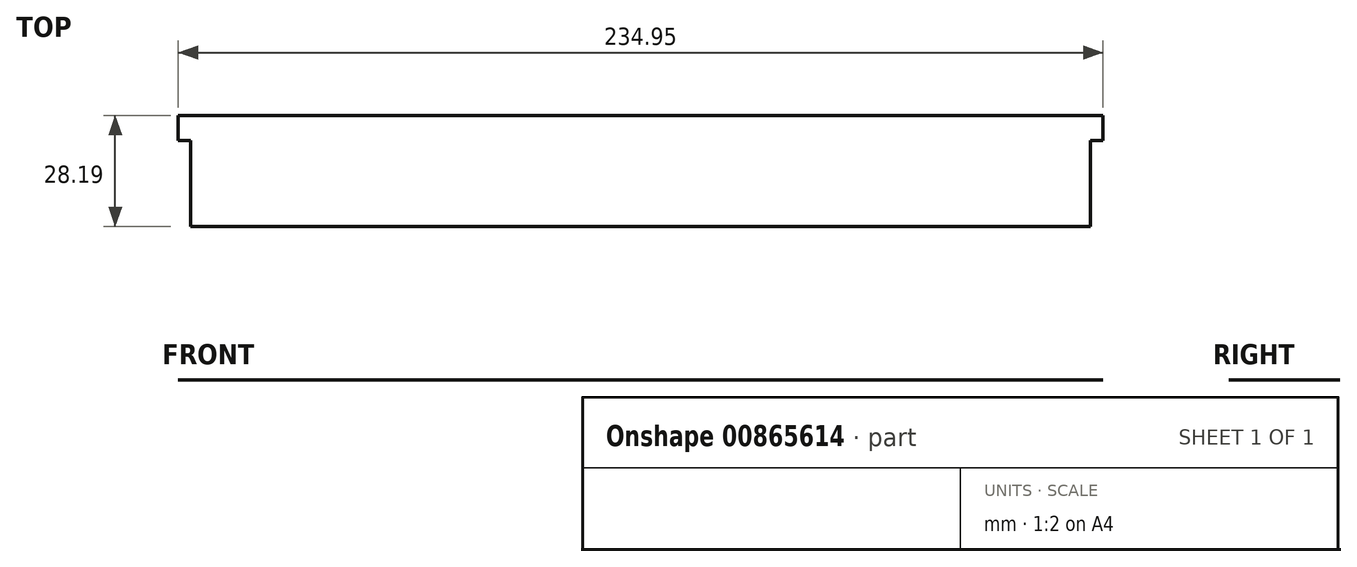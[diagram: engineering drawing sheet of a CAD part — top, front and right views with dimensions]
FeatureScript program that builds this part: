
annotation { "Feature Type Name" : "Feature", "Feature Type Description" : "" }
export const myFeature = defineFeature(function(context is Context, id is Id, definition is map)
    precondition{}
    {
        {
            var Q0;
            Q0=qCreatedBy(makeId("Top.planeOp"),FACE);
            var sketch = newSketch(context, id + "F0", { "sketchPlane" : qUnion([Q0])});
            skLineSegment(sketch, "E0.bottom", {"start": v(0, 0) * mm, "end": v(228.6, 0) * mm});
            skLineSegment(sketch, "E0.top", {"start": v(0, -28.2) * mm, "end": v(228.6, -28.2) * mm});
            skLineSegment(sketch, "E0.left", {"start": v(0, 0) * mm, "end": v(0, -28.2) * mm});
            skLineSegment(sketch, "E0.right", {"start": v(228.6, 0) * mm, "end": v(228.6, -28.2) * mm});
            skLineSegment(sketch, "E1.bottom", {"start": v(228.6, 0) * mm, "end": v(231.78, 0) * mm});
            skLineSegment(sketch, "E1.top", {"start": v(228.6, -6.35) * mm, "end": v(231.78, -6.35) * mm});
            skLineSegment(sketch, "E1.left", {"start": v(228.6, 0) * mm, "end": v(228.6, -6.35) * mm});
            skLineSegment(sketch, "E1.right", {"start": v(231.78, 0) * mm, "end": v(231.78, -6.35) * mm});
            skLineSegment(sketch, "E2.bottom", {"start": v(0, 0) * mm, "end": v(-3.17, 0) * mm});
            skLineSegment(sketch, "E2.top", {"start": v(0, -6.35) * mm, "end": v(-3.17, -6.35) * mm});
            skLineSegment(sketch, "E2.left", {"start": v(0, 0) * mm, "end": v(0, -6.35) * mm});
            skLineSegment(sketch, "E2.right", {"start": v(-3.17, 0) * mm, "end": v(-3.17, -6.35) * mm});
            skSolve(sketch);
        }
        {
            var Q0;
            Q0=makeQuery(id+"F0.imprint","IMPRINT",FACE,{"disambiguationData":[TD([[makeQuery(id+"F0.imprint","IMPRINT",EDGE,{"derivedFrom":sQuery(id+"F0.wireOp",EDGE,"E0.bottom")}),-1.0]])]});
            var Q1;
            Q1=makeQuery(id+"F0.imprint","IMPRINT",FACE,{"disambiguationData":[TD([[makeQuery(id+"F0.imprint","IMPRINT",EDGE,{"derivedFrom":sQuery(id+"F0.wireOp",EDGE,"E1.bottom")}),-1.0]])]});
            var Q2;
            Q2=makeQuery(id+"F0.imprint","IMPRINT",FACE,{"disambiguationData":[TD([[makeQuery(id+"F0.imprint","IMPRINT",EDGE,{"derivedFrom":sQuery(id+"F0.wireOp",EDGE,"E2.bottom")}),1.0]])]});
            extrude(context, id + "F1", {"entities" : qUnion([Q0, Q1, Q2]), "depth" : 1 / 203.2 * mm, "offsetDistance" : 25.4 * mm});
        }
    });
